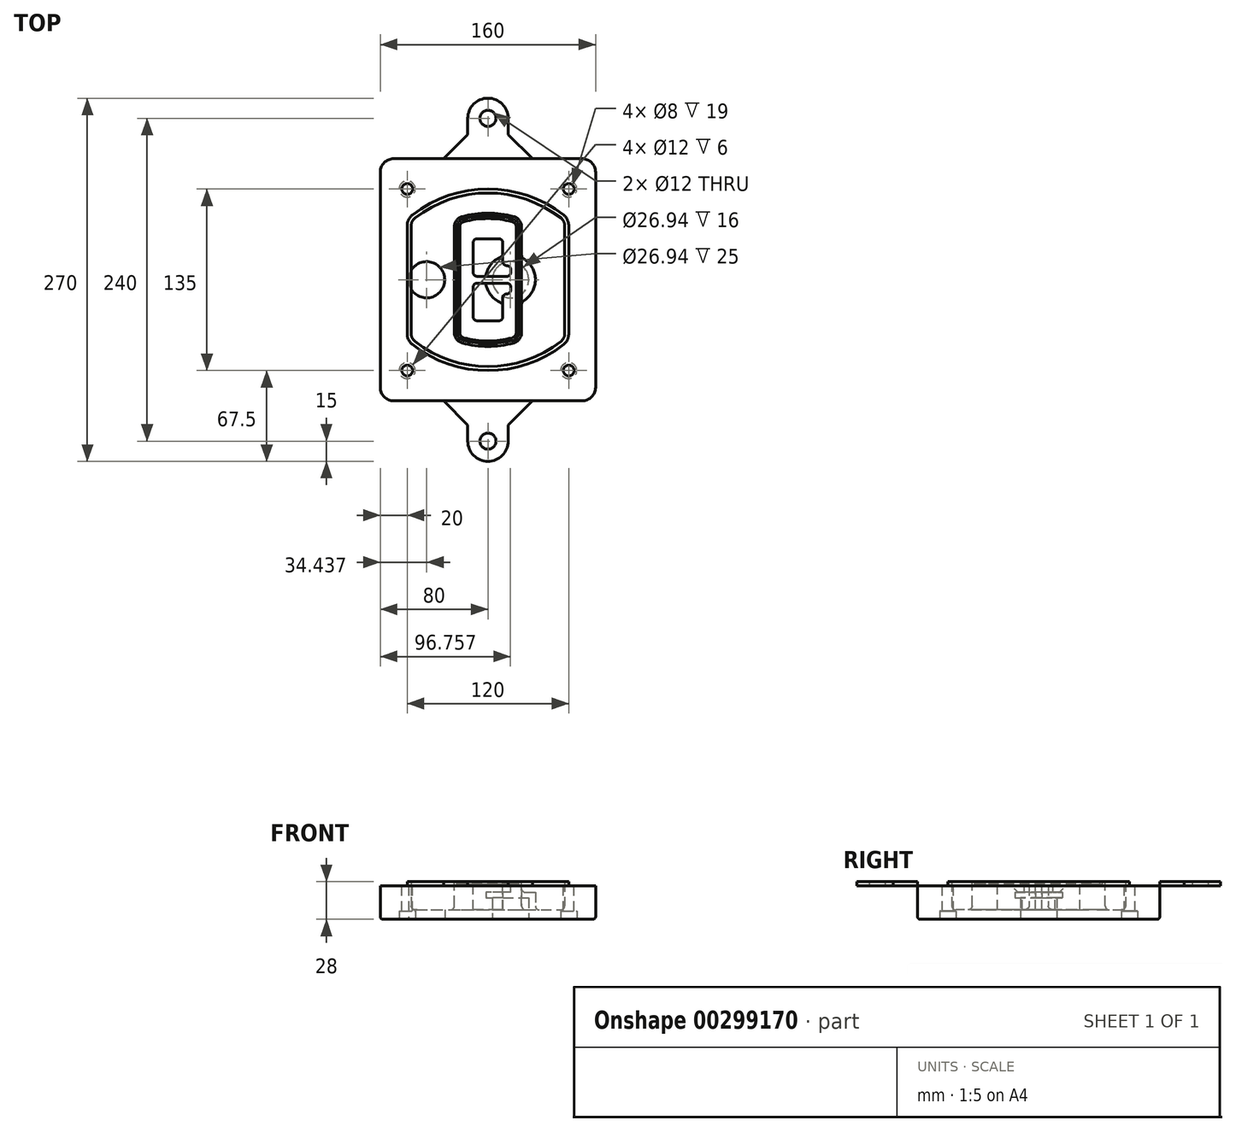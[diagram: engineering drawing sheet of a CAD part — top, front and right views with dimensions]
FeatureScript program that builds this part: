
annotation { "Feature Type Name" : "Feature", "Feature Type Description" : "" }
export const myFeature = defineFeature(function(context is Context, id is Id, definition is map)
    precondition{}
    {
        {
            var Q0;
            Q0=qCreatedBy(makeId("Top.planeOp"),FACE);
            var sketch = newSketch(context, id + "F0", { "sketchPlane" : qUnion([Q0])});
            skPoint(sketch, "E0.rect.middle", {"position": v(0, 0) * mm});
            skLineSegment(sketch, "E1.bottom", {"start": v(-70, -90) * mm, "end": v(70, -90) * mm});
            skLineSegment(sketch, "E1.top", {"start": v(-70, 90) * mm, "end": v(70, 90) * mm});
            skLineSegment(sketch, "E1.left", {"start": v(-80, -80) * mm, "end": v(-80, 80) * mm});
            skLineSegment(sketch, "E1.right", {"start": v(80, -80) * mm, "end": v(80, 80) * mm});
            skLineSegment(sketch, "E2", {"start": v(-80, 90) * mm, "end": v(80, -90) * mm, "construction": true});
            skLineSegment(sketch, "E3", {"start": v(80, 90) * mm, "end": v(-80, -90) * mm, "construction": true});
            skCircle(sketch, "E4", {"center": v(-60, 67.5) * mm, "radius": 4 * mm});
            skCircle(sketch, "E5", {"center": v(60, 67.5) * mm, "radius": 4 * mm});
            skCircle(sketch, "E6", {"center": v(60, -67.5) * mm, "radius": 4 * mm});
            skCircle(sketch, "E7", {"center": v(-60, -67.5) * mm, "radius": 4 * mm});
            skLineSegment(sketch, "E8", {"start": v(-60, 67.5) * mm, "end": v(60, 67.5) * mm, "construction": true});
            skLineSegment(sketch, "E9", {"start": v(60, 67.5) * mm, "end": v(60, -67.5) * mm, "construction": true});
            skLineSegment(sketch, "E10", {"start": v(60, -67.5) * mm, "end": v(-60, -67.5) * mm, "construction": true});
            skLineSegment(sketch, "E11", {"start": v(-60, -67.5) * mm, "end": v(-60, 67.5) * mm, "construction": true});
            skLineSegment(sketch, "E12", {"start": v(-60, 40.3) * mm, "end": v(-60, -40.3) * mm});
            skLineSegment(sketch, "E13", {"start": v(60, 40.3) * mm, "end": v(60, -40.3) * mm});
            skArc(sketch, "E14", {"start": v(56.15, 48.18) * mm, "mid": v(0, 67.5) * mm, "end": v(-56.15, 48.18) * mm});
            skArc(sketch, "E15", {"start": v(-56.15, -48.18) * mm, "mid": v(0, -67.5) * mm, "end": v(56.15, -48.18) * mm});
            skLineSegment(sketch, "E16", {"start": v(-60, 0) * mm, "end": v(60, 0) * mm, "construction": true});
            skPoint(sketch, "E17.visualSharp", {"position": v(-60, -45) * mm});
            skArc(sketch, "E17.filletArc", {"start": v(-60, -40.3) * mm, "mid": v(-58.99, -44.68) * mm, "end": v(-56.15, -48.18) * mm});
            skPoint(sketch, "E18.visualSharp", {"position": v(-60, 45) * mm});
            skArc(sketch, "E18.filletArc", {"start": v(-56.15, 48.18) * mm, "mid": v(-58.99, 44.68) * mm, "end": v(-60, 40.3) * mm});
            skPoint(sketch, "E19.visualSharp", {"position": v(60, 45) * mm});
            skArc(sketch, "E19.filletArc", {"start": v(60, 40.3) * mm, "mid": v(58.99, 44.68) * mm, "end": v(56.15, 48.18) * mm});
            skPoint(sketch, "E20.visualSharp", {"position": v(60, -45) * mm});
            skArc(sketch, "E20.filletArc", {"start": v(56.15, -48.18) * mm, "mid": v(58.99, -44.68) * mm, "end": v(60, -40.3) * mm});
            skPoint(sketch, "E21.visualSharp", {"position": v(-80, 90) * mm});
            skArc(sketch, "E21.filletArc", {"start": v(-70, 90) * mm, "mid": v(-77.07, 87.07) * mm, "end": v(-80, 80) * mm});
            skPoint(sketch, "E22.visualSharp", {"position": v(80, 90) * mm});
            skArc(sketch, "E22.filletArc", {"start": v(80, 80) * mm, "mid": v(77.07, 87.07) * mm, "end": v(70, 90) * mm});
            skPoint(sketch, "E23.visualSharp", {"position": v(80, -90) * mm});
            skArc(sketch, "E23.filletArc", {"start": v(70, -90) * mm, "mid": v(77.07, -87.07) * mm, "end": v(80, -80) * mm});
            skPoint(sketch, "E24.visualSharp", {"position": v(-80, -90) * mm});
            skArc(sketch, "E24.filletArc", {"start": v(-80, -80) * mm, "mid": v(-77.07, -87.07) * mm, "end": v(-70, -90) * mm});
            skArc(sketch, "E25.0", {"start": v(57, 40.3) * mm, "mid": v(56.3, 43.36) * mm, "end": v(54.3, 45.81) * mm});
            skLineSegment(sketch, "E25.1", {"start": v(57, 40.3) * mm, "end": v(57, -40.3) * mm});
            skArc(sketch, "E25.2", {"start": v(54.3, -45.81) * mm, "mid": v(56.3, -43.36) * mm, "end": v(57, -40.3) * mm});
            skArc(sketch, "E25.3", {"start": v(-54.3, -45.81) * mm, "mid": v(0, -64.5) * mm, "end": v(54.3, -45.81) * mm});
            skArc(sketch, "E25.4", {"start": v(-57, -40.3) * mm, "mid": v(-56.3, -43.36) * mm, "end": v(-54.3, -45.81) * mm});
            skArc(sketch, "E25.5", {"start": v(54.3, 45.81) * mm, "mid": v(0, 64.5) * mm, "end": v(-54.3, 45.81) * mm});
            skLineSegment(sketch, "E25.6", {"start": v(-57, 40.3) * mm, "end": v(-57, -40.3) * mm});
            skArc(sketch, "E25.7", {"start": v(-54.3, 45.81) * mm, "mid": v(-56.3, 43.36) * mm, "end": v(-57, 40.3) * mm});
            skArc(sketch, "E26.0", {"start": v(-58.62, 51.33) * mm, "mid": v(-62.58, 46.43) * mm, "end": v(-64, 40.3) * mm});
            skArc(sketch, "E26.1", {"start": v(58.62, 51.33) * mm, "mid": v(0, 71.5) * mm, "end": v(-58.62, 51.33) * mm});
            skArc(sketch, "E26.2", {"start": v(64, 40.3) * mm, "mid": v(62.58, 46.43) * mm, "end": v(58.62, 51.33) * mm});
            skLineSegment(sketch, "E26.3", {"start": v(64, 40.3) * mm, "end": v(64, -40.3) * mm});
            skArc(sketch, "E26.4", {"start": v(58.62, -51.33) * mm, "mid": v(62.58, -46.43) * mm, "end": v(64, -40.3) * mm});
            skLineSegment(sketch, "E26.5", {"start": v(-64, 40.3) * mm, "end": v(-64, -40.3) * mm});
            skArc(sketch, "E26.6", {"start": v(-58.62, -51.33) * mm, "mid": v(0, -71.5) * mm, "end": v(58.62, -51.33) * mm});
            skArc(sketch, "E26.7", {"start": v(-64, -40.3) * mm, "mid": v(-62.58, -46.43) * mm, "end": v(-58.62, -51.33) * mm});
            skSolve(sketch);
        }
        {
            var Q0;
            Q0=makeQuery(id+"F0.imprint","IMPRINT",FACE,{"disambiguationData":[TD([[makeQuery(id+"F0.imprint","IMPRINT",EDGE,{"derivedFrom":sQuery(id+"F0.wireOp",EDGE,"E1.bottom")}),1.0]])]});
            var Q1;
            Q1=makeQuery(id+"F0.imprint","IMPRINT",FACE,{"disambiguationData":[TD([[makeQuery(id+"F0.imprint","IMPRINT",EDGE,{"derivedFrom":sQuery(id+"F0.wireOp",EDGE,"E12")}),1.0]])]});
            var Q2;
            Q2=makeQuery(id+"F0.imprint","IMPRINT",FACE,{"disambiguationData":[TD([[makeQuery(id+"F0.imprint","IMPRINT",EDGE,{"derivedFrom":sQuery(id+"F0.wireOp",EDGE,"E25.0")}),1.0]])]});
            var Q3;
            Q3=makeQuery(id+"F0.imprint","IMPRINT",FACE,{"disambiguationData":[TD([[makeQuery(id+"F0.imprint","IMPRINT",EDGE,{"derivedFrom":sQuery(id+"F0.wireOp",EDGE,"E12")}),-1.0]])]});
            extrude(context, id + "F1", {"entities" : qUnion([Q0, Q1, Q2, Q3]), "oppositeDirection" : true, "depth" : 25 * mm});
        }
        {
            var Q0;
            Q0=makeQuery(id+"F0.imprint","IMPRINT",FACE,{"disambiguationData":[TD([[makeQuery(id+"F0.imprint","IMPRINT",EDGE,{"derivedFrom":sQuery(id+"F0.wireOp",EDGE,"E12")}),1.0]])]});
            extrude(context, id + "F2", {"entities" : qUnion([Q0]), "operationType" : NewBodyOperationType.ADD, "depth" : 3 * mm});
        }
        {
            var Q0;
            Q0=makeQuery(id+"F0.imprint","IMPRINT",FACE,{"disambiguationData":[TD([[makeQuery(id+"F0.imprint","IMPRINT",EDGE,{"derivedFrom":sQuery(id+"F0.wireOp",EDGE,"E25.0")}),1.0]])]});
            extrude(context, id + "F3", {"entities" : qUnion([Q0]), "operationType" : NewBodyOperationType.REMOVE, "oppositeDirection" : true, "depth" : 18 * mm});
        }
        {
            var Q0;
            Q0=makeQuery(id+"F2.opExtrude","CAP_FACE",FACE,{"disambiguationData":[OSD([sQuery(id+"F0.wireOp",EDGE,"E12"),sQuery(id+"F0.wireOp",EDGE,"E13"),sQuery(id+"F0.wireOp",EDGE,"E14"),sQuery(id+"F0.wireOp",EDGE,"E15"),sQuery(id+"F0.wireOp",EDGE,"E17.filletArc"),sQuery(id+"F0.wireOp",EDGE,"E18.filletArc"),sQuery(id+"F0.wireOp",EDGE,"E19.filletArc"),sQuery(id+"F0.wireOp",EDGE,"E20.filletArc"),sQuery(id+"F0.wireOp",EDGE,"E25.0"),sQuery(id+"F0.wireOp",EDGE,"E25.1"),sQuery(id+"F0.wireOp",EDGE,"E25.2"),sQuery(id+"F0.wireOp",EDGE,"E25.3"),sQuery(id+"F0.wireOp",EDGE,"E25.4"),sQuery(id+"F0.wireOp",EDGE,"E25.5"),sQuery(id+"F0.wireOp",EDGE,"E25.6"),sQuery(id+"F0.wireOp",EDGE,"E25.7")])],"isStart":false});
            var sketch = newSketch(context, id + "F4", { "sketchPlane" : qUnion([Q0])});
            skArc(sketch, "E27.0", {"start": v(-19.08, -46.97) * mm, "mid": v(0, -49.5) * mm, "end": v(19.08, -46.97) * mm});
            skArc(sketch, "E28.0", {"start": v(19.08, 46.97) * mm, "mid": v(0, 49.5) * mm, "end": v(-19.08, 46.97) * mm});
            skLineSegment(sketch, "E29", {"start": v(-25, 39.25) * mm, "end": v(-25, -39.25) * mm});
            skLineSegment(sketch, "E30", {"start": v(25, 39.25) * mm, "end": v(25, -39.25) * mm});
            skLineSegment(sketch, "E31", {"start": v(-25, 45.1) * mm, "end": v(25, 45.1) * mm, "construction": true});
            skLineSegment(sketch, "E32", {"start": v(-25, -45.1) * mm, "end": v(25, -45.1) * mm, "construction": true});
            skPoint(sketch, "E33.visualSharp", {"position": v(-25, 45.1) * mm});
            skArc(sketch, "E33.filletArc", {"start": v(-19.08, 46.97) * mm, "mid": v(-23.35, 44.11) * mm, "end": v(-25, 39.25) * mm});
            skPoint(sketch, "E34.visualSharp", {"position": v(25, 45.1) * mm});
            skArc(sketch, "E34.filletArc", {"start": v(25, 39.25) * mm, "mid": v(23.35, 44.11) * mm, "end": v(19.08, 46.97) * mm});
            skPoint(sketch, "E35.visualSharp", {"position": v(25, -45.1) * mm});
            skArc(sketch, "E35.filletArc", {"start": v(19.08, -46.97) * mm, "mid": v(23.35, -44.11) * mm, "end": v(25, -39.25) * mm});
            skPoint(sketch, "E36.visualSharp", {"position": v(-25, -45.1) * mm});
            skArc(sketch, "E36.filletArc", {"start": v(-25, -39.25) * mm, "mid": v(-23.35, -44.11) * mm, "end": v(-19.08, -46.97) * mm});
            skArc(sketch, "E37.0", {"start": v(54.3, 45.81) * mm, "mid": v(0, 64.5) * mm, "end": v(-54.3, 45.81) * mm});
            skArc(sketch, "E37.1", {"start": v(-54.3, 45.81) * mm, "mid": v(-56.3, 43.36) * mm, "end": v(-57, 40.3) * mm});
            skLineSegment(sketch, "E37.2", {"start": v(-57, 40.3) * mm, "end": v(-57, -40.3) * mm});
            skArc(sketch, "E37.3", {"start": v(-57, -40.3) * mm, "mid": v(-56.3, -43.36) * mm, "end": v(-54.3, -45.81) * mm});
            skArc(sketch, "E37.4", {"start": v(-54.3, -45.81) * mm, "mid": v(0, -64.5) * mm, "end": v(54.3, -45.81) * mm});
            skArc(sketch, "E37.5", {"start": v(54.3, -45.81) * mm, "mid": v(56.3, -43.36) * mm, "end": v(57, -40.3) * mm});
            skLineSegment(sketch, "E37.6", {"start": v(57, 40.3) * mm, "end": v(57, -40.3) * mm});
            skArc(sketch, "E37.7", {"start": v(57, 40.3) * mm, "mid": v(56.3, 43.36) * mm, "end": v(54.3, 45.81) * mm});
            skLineSegment(sketch, "E38.0", {"start": v(23, 39.25) * mm, "end": v(23, -39.25) * mm});
            skArc(sketch, "E38.1", {"start": v(18.56, -45.04) * mm, "mid": v(21.76, -42.9) * mm, "end": v(23, -39.25) * mm});
            skArc(sketch, "E38.2", {"start": v(-18.56, -45.04) * mm, "mid": v(0, -47.5) * mm, "end": v(18.56, -45.04) * mm});
            skArc(sketch, "E38.3", {"start": v(-23, -39.25) * mm, "mid": v(-21.76, -42.9) * mm, "end": v(-18.56, -45.04) * mm});
            skLineSegment(sketch, "E38.4", {"start": v(-23, 39.25) * mm, "end": v(-23, -39.25) * mm});
            skArc(sketch, "E38.5", {"start": v(23, 39.25) * mm, "mid": v(21.76, 42.9) * mm, "end": v(18.56, 45.04) * mm});
            skArc(sketch, "E38.6", {"start": v(-18.56, 45.04) * mm, "mid": v(-21.76, 42.9) * mm, "end": v(-23, 39.25) * mm});
            skArc(sketch, "E38.7", {"start": v(18.56, 45.04) * mm, "mid": v(0, 47.5) * mm, "end": v(-18.56, 45.04) * mm});
            skArc(sketch, "E39.0", {"start": v(21, 39.25) * mm, "mid": v(20.18, 41.68) * mm, "end": v(18.04, 43.1) * mm});
            skLineSegment(sketch, "E39.1", {"start": v(21, 39.25) * mm, "end": v(21, -39.25) * mm});
            skArc(sketch, "E39.2", {"start": v(18.04, -43.1) * mm, "mid": v(20.18, -41.68) * mm, "end": v(21, -39.25) * mm});
            skArc(sketch, "E39.3", {"start": v(-18.04, -43.1) * mm, "mid": v(0, -45.5) * mm, "end": v(18.04, -43.1) * mm});
            skArc(sketch, "E39.4", {"start": v(-21, -39.25) * mm, "mid": v(-20.18, -41.68) * mm, "end": v(-18.04, -43.1) * mm});
            skArc(sketch, "E39.5", {"start": v(18.04, 43.1) * mm, "mid": v(0, 45.5) * mm, "end": v(-18.04, 43.1) * mm});
            skLineSegment(sketch, "E39.6", {"start": v(-21, 39.25) * mm, "end": v(-21, -39.25) * mm});
            skArc(sketch, "E39.7", {"start": v(-18.04, 43.1) * mm, "mid": v(-20.18, 41.68) * mm, "end": v(-21, 39.25) * mm});
            skLineSegment(sketch, "E40", {"start": v(-25, 0) * mm, "end": v(25, 0) * mm, "construction": true});
            skLineSegment(sketch, "E41", {"start": v(-11, 5.5) * mm, "end": v(-11, 27.5) * mm});
            skLineSegment(sketch, "E42", {"start": v(-8, 30.5) * mm, "end": v(8, 30.5) * mm});
            skLineSegment(sketch, "E43", {"start": v(11, 27.5) * mm, "end": v(11, 13.5) * mm});
            skLineSegment(sketch, "E44", {"start": v(14, 10.5) * mm, "end": v(14, 10.5) * mm});
            skLineSegment(sketch, "E45", {"start": v(17, 7.5) * mm, "end": v(17, 5.5) * mm});
            skLineSegment(sketch, "E46", {"start": v(14, 2.5) * mm, "end": v(-8, 2.5) * mm});
            skPoint(sketch, "E47.visualSharp", {"position": v(-11, 30.5) * mm});
            skArc(sketch, "E47.filletArc", {"start": v(-8, 30.5) * mm, "mid": v(-10.12, 29.62) * mm, "end": v(-11, 27.5) * mm});
            skPoint(sketch, "E48.visualSharp", {"position": v(11, 30.5) * mm});
            skArc(sketch, "E48.filletArc", {"start": v(11, 27.5) * mm, "mid": v(10.12, 29.62) * mm, "end": v(8, 30.5) * mm});
            skPoint(sketch, "E49.visualSharp", {"position": v(11, 10.5) * mm});
            skArc(sketch, "E49.filletArc", {"start": v(11, 13.5) * mm, "mid": v(11.88, 11.38) * mm, "end": v(14, 10.5) * mm});
            skPoint(sketch, "E50.visualSharp", {"position": v(17, 10.5) * mm});
            skArc(sketch, "E50.filletArc", {"start": v(17, 7.5) * mm, "mid": v(16.12, 9.62) * mm, "end": v(14, 10.5) * mm});
            skPoint(sketch, "E51.visualSharp", {"position": v(17, 2.5) * mm});
            skArc(sketch, "E51.filletArc", {"start": v(14, 2.5) * mm, "mid": v(16.12, 3.38) * mm, "end": v(17, 5.5) * mm});
            skPoint(sketch, "E52.visualSharp", {"position": v(-11, 2.5) * mm});
            skArc(sketch, "E52.filletArc", {"start": v(-11, 5.5) * mm, "mid": v(-10.12, 3.38) * mm, "end": v(-8, 2.5) * mm});
            skLineSegment(sketch, "E53.0.MirrorCS", {"start": v(14, -2.5) * mm, "end": v(-8, -2.5) * mm});
            skArc(sketch, "E54.0.MirrorCS", {"start": v(-11, -5.5) * mm, "mid": v(-10.12, -3.38) * mm, "end": v(-8, -2.5) * mm});
            skLineSegment(sketch, "E55.0.MirrorCS", {"start": v(-11, -5.5) * mm, "end": v(-11, -27.5) * mm});
            skArc(sketch, "E56.0.MirrorCS", {"start": v(-8, -30.5) * mm, "mid": v(-10.12, -29.62) * mm, "end": v(-11, -27.5) * mm});
            skLineSegment(sketch, "E57.0.MirrorCS", {"start": v(-8, -30.5) * mm, "end": v(8, -30.5) * mm});
            skArc(sketch, "E58.0.MirrorCS", {"start": v(11, -27.5) * mm, "mid": v(10.12, -29.62) * mm, "end": v(8, -30.5) * mm});
            skLineSegment(sketch, "E59.0.MirrorCS", {"start": v(11, -27.5) * mm, "end": v(11, -13.5) * mm});
            skArc(sketch, "E60.0.MirrorCS", {"start": v(11, -13.5) * mm, "mid": v(11.88, -11.38) * mm, "end": v(14, -10.5) * mm});
            skArc(sketch, "E61.0.MirrorCS", {"start": v(17, -7.5) * mm, "mid": v(16.12, -9.62) * mm, "end": v(14, -10.5) * mm});
            skLineSegment(sketch, "E62.0.MirrorCS", {"start": v(17, -7.5) * mm, "end": v(17, -5.5) * mm});
            skArc(sketch, "E63.0.MirrorCS", {"start": v(14, -2.5) * mm, "mid": v(16.12, -3.38) * mm, "end": v(17, -5.5) * mm});
            skSolve(sketch);
        }
        {
            var Q0;
            Q0=makeQuery(id+"F4.imprint","IMPRINT",FACE,{"disambiguationData":[TD([[makeQuery(id+"F4.imprint","IMPRINT",EDGE,{"derivedFrom":sQuery(id+"F4.wireOp",EDGE,"E27.0")}),1.0]])]});
            var Q1;
            Q1=makeQuery(id+"F4.imprint","IMPRINT",FACE,{"disambiguationData":[TD([[makeQuery(id+"F4.imprint","IMPRINT",EDGE,{"derivedFrom":sQuery(id+"F4.wireOp",EDGE,"E38.0")}),-1.0]])]});
            var Q2;
            Q2=makeQuery(id+"F4.imprint","IMPRINT",FACE,{"disambiguationData":[TD([[makeQuery(id+"F4.imprint","IMPRINT",EDGE,{"derivedFrom":sQuery(id+"F4.wireOp",EDGE,"E39.0")}),1.0]])]});
            extrude(context, id + "F5", {"entities" : qUnion([Q0, Q1, Q2]), "operationType" : NewBodyOperationType.ADD, "endBound" : BoundingType.UP_TO_NEXT, "oppositeDirection" : true, "depth" : 25 * mm});
        }
        {
            var Q0;
            Q0=makeQuery(id+"F4.imprint","IMPRINT",FACE,{"disambiguationData":[TD([[makeQuery(id+"F4.imprint","IMPRINT",EDGE,{"derivedFrom":sQuery(id+"F4.wireOp",EDGE,"E38.0")}),-1.0]])]});
            extrude(context, id + "F6", {"entities" : qUnion([Q0]), "operationType" : NewBodyOperationType.REMOVE, "oppositeDirection" : true, "depth" : 2 * mm});
        }
        {
            var Q0;
            Q0=makeQuery(id+"F1.opExtrude","CAP_FACE",FACE,{"disambiguationData":[OSD([sQuery(id+"F0.wireOp",EDGE,"E1.bottom"),sQuery(id+"F0.wireOp",EDGE,"E1.top"),sQuery(id+"F0.wireOp",EDGE,"E1.left"),sQuery(id+"F0.wireOp",EDGE,"E1.right"),sQuery(id+"F0.wireOp",EDGE,"E4"),sQuery(id+"F0.wireOp",EDGE,"E5"),sQuery(id+"F0.wireOp",EDGE,"E6"),sQuery(id+"F0.wireOp",EDGE,"E7"),sQuery(id+"F0.wireOp",EDGE,"E21.filletArc"),sQuery(id+"F0.wireOp",EDGE,"E22.filletArc"),sQuery(id+"F0.wireOp",EDGE,"E23.filletArc"),sQuery(id+"F0.wireOp",EDGE,"E24.filletArc")])],"isStart":false});
            var sketch = newSketch(context, id + "F7", { "sketchPlane" : qUnion([Q0])});
            skCircle(sketch, "E64", {"center": v(16.76, 0) * mm, "radius": 13.47 * mm});
            skCircle(sketch, "E65", {"center": v(-45.56, 0) * mm, "radius": 13.47 * mm});
            skLineSegment(sketch, "E66", {"start": v(80, 0) * mm, "end": v(-80, 0) * mm});
            skCircle(sketch, "E67", {"center": v(16.76, 0) * mm, "radius": 18.47 * mm});
            skCircle(sketch, "E68", {"center": v(60, -67.5) * mm, "radius": 6 * mm});
            skCircle(sketch, "E69", {"center": v(-60, -67.5) * mm, "radius": 6 * mm});
            skCircle(sketch, "E70", {"center": v(-60, 67.5) * mm, "radius": 6 * mm});
            skCircle(sketch, "E71", {"center": v(60, 67.5) * mm, "radius": 6 * mm});
            skSolve(sketch);
        }
        {
            var Q0;
            {var subQ1=sQuery(id+"F7.wireOp",EDGE,"E66");var subQ4=sQuery(id+"F7.wireOp",EDGE,"E64");var subQ6=makeQuery(id+"F7.imprint","INTERSECT",VERTEX,{"disambiguationData":[OD(0.0)],"derivedFrom":[subQ4,subQ1]});Q0=makeQuery(id+"F7.imprint","IMPRINT",FACE,{"disambiguationData":[TD([[makeQuery(id+"F7.imprint","IMPRINT",EDGE,{"disambiguationData":[TD([[subQ6,-1.0]])],"derivedFrom":subQ4}),-1.0]])]});}
            var Q1;
            {var subQ0=sQuery(id+"F7.wireOp",EDGE,"E66");var subQ1=sQuery(id+"F7.wireOp",EDGE,"E64");var subQ3=makeQuery(id+"F7.imprint","INTERSECT",VERTEX,{"disambiguationData":[OD(0.0)],"derivedFrom":[subQ1,subQ0]});Q1=makeQuery(id+"F7.imprint","IMPRINT",FACE,{"disambiguationData":[TD([[makeQuery(id+"F7.imprint","IMPRINT",EDGE,{"disambiguationData":[TD([[subQ3,-1.0]])],"derivedFrom":subQ1}),1.0]])]});}
            var Q2;
            {var subQ0=sQuery(id+"F7.wireOp",EDGE,"E66");var subQ1=sQuery(id+"F7.wireOp",EDGE,"E64");var subQ3=makeQuery(id+"F7.imprint","INTERSECT",VERTEX,{"disambiguationData":[OD(0.0)],"derivedFrom":[subQ1,subQ0]});Q2=makeQuery(id+"F7.imprint","IMPRINT",FACE,{"disambiguationData":[TD([[makeQuery(id+"F7.imprint","IMPRINT",EDGE,{"disambiguationData":[TD([[subQ3,1.0]])],"derivedFrom":subQ1}),1.0]])]});}
            var Q3;
            {var subQ1=sQuery(id+"F7.wireOp",EDGE,"E66");var subQ4=sQuery(id+"F7.wireOp",EDGE,"E64");var subQ6=makeQuery(id+"F7.imprint","INTERSECT",VERTEX,{"disambiguationData":[OD(0.0)],"derivedFrom":[subQ4,subQ1]});Q3=makeQuery(id+"F7.imprint","IMPRINT",FACE,{"disambiguationData":[TD([[makeQuery(id+"F7.imprint","IMPRINT",EDGE,{"disambiguationData":[TD([[subQ6,1.0]])],"derivedFrom":subQ4}),-1.0]])]});}
            extrude(context, id + "F8", {"entities" : qUnion([Q0, Q1, Q2, Q3]), "operationType" : NewBodyOperationType.ADD, "oppositeDirection" : true, "depth" : 20 * mm});
        }
        {
            var Q0;
            {var subQ0=sQuery(id+"F7.wireOp",EDGE,"E66");var subQ1=sQuery(id+"F7.wireOp",EDGE,"E64");var subQ3=makeQuery(id+"F7.imprint","INTERSECT",VERTEX,{"disambiguationData":[OD(0.0)],"derivedFrom":[subQ1,subQ0]});Q0=makeQuery(id+"F7.imprint","IMPRINT",FACE,{"disambiguationData":[TD([[makeQuery(id+"F7.imprint","IMPRINT",EDGE,{"disambiguationData":[TD([[subQ3,-1.0]])],"derivedFrom":subQ1}),1.0]])]});}
            var Q1;
            {var subQ0=sQuery(id+"F7.wireOp",EDGE,"E66");var subQ1=sQuery(id+"F7.wireOp",EDGE,"E64");var subQ3=makeQuery(id+"F7.imprint","INTERSECT",VERTEX,{"disambiguationData":[OD(0.0)],"derivedFrom":[subQ1,subQ0]});Q1=makeQuery(id+"F7.imprint","IMPRINT",FACE,{"disambiguationData":[TD([[makeQuery(id+"F7.imprint","IMPRINT",EDGE,{"disambiguationData":[TD([[subQ3,1.0]])],"derivedFrom":subQ1}),1.0]])]});}
            extrude(context, id + "F9", {"entities" : qUnion([Q0, Q1]), "operationType" : NewBodyOperationType.REMOVE, "oppositeDirection" : true, "depth" : 16 * mm});
        }
        {
            var Q0;
            {var subQ0=sQuery(id+"F7.wireOp",EDGE,"E66");var subQ1=sQuery(id+"F7.wireOp",EDGE,"E65");var subQ3=makeQuery(id+"F7.imprint","INTERSECT",VERTEX,{"disambiguationData":[OD(0.0)],"derivedFrom":[subQ1,subQ0]});Q0=makeQuery(id+"F7.imprint","IMPRINT",FACE,{"disambiguationData":[TD([[makeQuery(id+"F7.imprint","IMPRINT",EDGE,{"disambiguationData":[TD([[subQ3,-1.0]])],"derivedFrom":subQ1}),1.0]])]});}
            var Q1;
            {var subQ0=sQuery(id+"F7.wireOp",EDGE,"E66");var subQ1=sQuery(id+"F7.wireOp",EDGE,"E65");var subQ3=makeQuery(id+"F7.imprint","INTERSECT",VERTEX,{"disambiguationData":[OD(0.0)],"derivedFrom":[subQ1,subQ0]});Q1=makeQuery(id+"F7.imprint","IMPRINT",FACE,{"disambiguationData":[TD([[makeQuery(id+"F7.imprint","IMPRINT",EDGE,{"disambiguationData":[TD([[subQ3,1.0]])],"derivedFrom":subQ1}),1.0]])]});}
            extrude(context, id + "F10", {"entities" : qUnion([Q0, Q1]), "operationType" : NewBodyOperationType.REMOVE, "oppositeDirection" : true, "depth" : 25 * mm});
        }
        {
            var Q0;
            Q0=makeQuery(id+"F7.imprint","IMPRINT",FACE,{"disambiguationData":[TD([[makeQuery(id+"F7.imprint","IMPRINT",EDGE,{"derivedFrom":sQuery(id+"F7.wireOp",EDGE,"E68")}),1.0]])]});
            var Q1;
            Q1=makeQuery(id+"F7.imprint","IMPRINT",FACE,{"disambiguationData":[TD([[makeQuery(id+"F7.imprint","IMPRINT",EDGE,{"derivedFrom":makeQuery(id+"F1.opExtrude","CAP_EDGE",EDGE,{"disambiguationData":[OSD([sQuery(id+"F0.wireOp",EDGE,"E5")])],"isStart":false})}),-1.0]])]});
            var Q2;
            Q2=makeQuery(id+"F7.imprint","IMPRINT",FACE,{"disambiguationData":[TD([[makeQuery(id+"F7.imprint","IMPRINT",EDGE,{"derivedFrom":sQuery(id+"F7.wireOp",EDGE,"E69")}),1.0]])]});
            var Q3;
            Q3=makeQuery(id+"F7.imprint","IMPRINT",FACE,{"disambiguationData":[TD([[makeQuery(id+"F7.imprint","IMPRINT",EDGE,{"derivedFrom":makeQuery(id+"F1.opExtrude","CAP_EDGE",EDGE,{"disambiguationData":[OSD([sQuery(id+"F0.wireOp",EDGE,"E4")])],"isStart":false})}),-1.0]])]});
            var Q4;
            Q4=makeQuery(id+"F7.imprint","IMPRINT",FACE,{"disambiguationData":[TD([[makeQuery(id+"F7.imprint","IMPRINT",EDGE,{"derivedFrom":sQuery(id+"F7.wireOp",EDGE,"E70")}),1.0]])]});
            var Q5;
            Q5=makeQuery(id+"F7.imprint","IMPRINT",FACE,{"disambiguationData":[TD([[makeQuery(id+"F7.imprint","IMPRINT",EDGE,{"derivedFrom":makeQuery(id+"F1.opExtrude","CAP_EDGE",EDGE,{"disambiguationData":[OSD([sQuery(id+"F0.wireOp",EDGE,"E7")])],"isStart":false})}),-1.0]])]});
            var Q6;
            Q6=makeQuery(id+"F7.imprint","IMPRINT",FACE,{"disambiguationData":[TD([[makeQuery(id+"F7.imprint","IMPRINT",EDGE,{"derivedFrom":sQuery(id+"F7.wireOp",EDGE,"E71")}),1.0]])]});
            var Q7;
            Q7=makeQuery(id+"F7.imprint","IMPRINT",FACE,{"disambiguationData":[TD([[makeQuery(id+"F7.imprint","IMPRINT",EDGE,{"derivedFrom":makeQuery(id+"F1.opExtrude","CAP_EDGE",EDGE,{"disambiguationData":[OSD([sQuery(id+"F0.wireOp",EDGE,"E6")])],"isStart":false})}),-1.0]])]});
            extrude(context, id + "F11", {"entities" : qUnion([Q0, Q1, Q2, Q3, Q4, Q5, Q6, Q7]), "operationType" : NewBodyOperationType.REMOVE, "oppositeDirection" : true, "depth" : 6 * mm});
        }
        {
            var Q0;
            Q0=makeQuery(id+"F9.boolean.opBoolean","COPY",FACE,{"derivedFrom":makeQuery(id+"F9.opExtrude","CAP_FACE",FACE,{"disambiguationData":[OSD([sQuery(id+"F7.wireOp",EDGE,"E64")])],"isStart":false})});
            var sketch = newSketch(context, id + "F12", { "sketchPlane" : qUnion([Q0])});
            skArc(sketch, "E72.0", {"start": v(11, 17.55) * mm, "mid": v(2.57, 11.82) * mm, "end": v(-1.54, 2.5) * mm});
            skArc(sketch, "E72.1", {"start": v(-1.54, -2.5) * mm, "mid": v(2.57, -11.82) * mm, "end": v(11, -17.55) * mm});
            skLineSegment(sketch, "E73", {"start": v(-1.54, -2.5) * mm, "end": v(14, -2.5) * mm});
            skLineSegment(sketch, "E74.0", {"start": v(14, 2.5) * mm, "end": v(-1.54, 2.5) * mm});
            skArc(sketch, "E74.1", {"start": v(14, 2.5) * mm, "mid": v(16.12, 3.38) * mm, "end": v(17, 5.5) * mm});
            skLineSegment(sketch, "E74.2", {"start": v(17, 7.5) * mm, "end": v(17, 5.5) * mm});
            skArc(sketch, "E74.3", {"start": v(17, 7.5) * mm, "mid": v(16.12, 9.62) * mm, "end": v(14, 10.5) * mm});
            skArc(sketch, "E74.4", {"start": v(11, 13.5) * mm, "mid": v(11.88, 11.38) * mm, "end": v(14, 10.5) * mm});
            skLineSegment(sketch, "E74.5", {"start": v(11, 17.55) * mm, "end": v(11, 13.5) * mm});
            skLineSegment(sketch, "E74.7", {"start": v(14, -2.5) * mm, "end": v(-1.54, -2.5) * mm});
            skArc(sketch, "E74.8", {"start": v(14, -2.5) * mm, "mid": v(16.12, -3.38) * mm, "end": v(17, -5.5) * mm});
            skLineSegment(sketch, "E74.9", {"start": v(17, -7.5) * mm, "end": v(17, -5.5) * mm});
            skArc(sketch, "E74.10", {"start": v(17, -7.5) * mm, "mid": v(16.12, -9.62) * mm, "end": v(14, -10.5) * mm});
            skArc(sketch, "E74.11", {"start": v(11, -13.5) * mm, "mid": v(11.88, -11.38) * mm, "end": v(14, -10.5) * mm});
            skLineSegment(sketch, "E74.12", {"start": v(11, -17.55) * mm, "end": v(11, -13.5) * mm});
            skPoint(sketch, "E75.orphan", {"position": v(11, -27.5) * mm});
            skPoint(sketch, "E76.orphan", {"position": v(-8, -2.5) * mm});
            skPoint(sketch, "E77.orphan", {"position": v(-8, 2.5) * mm});
            skPoint(sketch, "E78.orphan", {"position": v(11, 27.5) * mm});
            skSolve(sketch);
        }
        {
            var Q0;
            {var subQ7=sQuery(id+"F12.wireOp",EDGE,"E72.0");var subQ14=sQuery(id+"F12.wireOp",EDGE,"E72.1");var subQ16=sQuery(id+"F12.wireOp",EDGE,"E74.1");var subQ18=sQuery(id+"F12.wireOp",EDGE,"E74.8");Q0=qUnion([makeQuery(id+"F12.imprint","IMPRINT",FACE,{"disambiguationData":[TD([[makeQuery(id+"F12.imprint","IMPRINT",EDGE,{"derivedFrom":subQ7}),1.0]])]}),makeQuery(id+"F12.imprint","IMPRINT",FACE,{"disambiguationData":[TD([[makeQuery(id+"F12.imprint","IMPRINT",EDGE,{"derivedFrom":subQ14}),1.0]])]}),makeQuery(id+"F12.imprint","IMPRINT",FACE,{"disambiguationData":[TD([[makeQuery(id+"F12.imprint","IMPRINT",EDGE,{"derivedFrom":subQ16}),1.0]])]}),makeQuery(id+"F12.imprint","IMPRINT",FACE,{"disambiguationData":[TD([[makeQuery(id+"F12.imprint","IMPRINT",EDGE,{"derivedFrom":subQ18}),-1.0]])]})]);}
            var Q1;
            Q1=makeQuery(id+"F5.boolean.opBoolean","SPLIT",FACE,{"disambiguationData":[TD([makeQuery(id+"F5.opExtrude","SWEPT_FACE",FACE,{"disambiguationData":[OSD([sQuery(id+"F4.wireOp",EDGE,"E41")])]})])],"derivedFrom":makeQuery(id+"F3.boolean.opBoolean","COPY",FACE,{"derivedFrom":makeQuery(id+"F3.opExtrude","CAP_FACE",FACE,{"disambiguationData":[OSD([sQuery(id+"F0.wireOp",EDGE,"E25.0"),sQuery(id+"F0.wireOp",EDGE,"E25.1"),sQuery(id+"F0.wireOp",EDGE,"E25.2"),sQuery(id+"F0.wireOp",EDGE,"E25.3"),sQuery(id+"F0.wireOp",EDGE,"E25.4"),sQuery(id+"F0.wireOp",EDGE,"E25.5"),sQuery(id+"F0.wireOp",EDGE,"E25.6"),sQuery(id+"F0.wireOp",EDGE,"E25.7")])],"isStart":false})})});
            extrude(context, id + "F13", {"entities" : qUnion([Q0]), "operationType" : NewBodyOperationType.REMOVE, "endBound" : BoundingType.UP_TO_SURFACE, "endBoundEntityFace" : qUnion([Q1]), "depth" : 25 * mm});
        }
        {
            var Q0;
            Q0=makeQuery(id+"F3.boolean.opBoolean","COPY",EDGE,{"derivedFrom":makeQuery(id+"F3.opExtrude","CAP_EDGE",EDGE,{"disambiguationData":[OSD([sQuery(id+"F0.wireOp",EDGE,"E25.6")])],"isStart":false})});
            var Q1;
            Q1=makeQuery(id+"F8.boolean.opBoolean","INTERSECT",EDGE,{"derivedFrom":[makeQuery(id+"F5.opExtrude","SWEPT_FACE",FACE,{"disambiguationData":[OSD([sQuery(id+"F4.wireOp",EDGE,"E30")])]}),makeQuery(id+"F8.opExtrude","CAP_FACE",FACE,{"disambiguationData":[OSD([sQuery(id+"F7.wireOp",EDGE,"E67")])],"isStart":false})]});
            var Q2;
            Q2=makeQuery(id+"F8.boolean.opBoolean","INTERSECT",EDGE,{"disambiguationData":[OD(1.0)],"derivedFrom":[makeQuery(id+"F5.opExtrude","SWEPT_FACE",FACE,{"disambiguationData":[OSD([sQuery(id+"F4.wireOp",EDGE,"E30")])]}),makeQuery(id+"F8.opExtrude","SWEPT_FACE",FACE,{"disambiguationData":[OSD([sQuery(id+"F7.wireOp",EDGE,"E67")])]})]});
            var Q3;
            {var subQ0=sQuery(id+"F4.wireOp",EDGE,"E30");Q3=makeQuery(id+"F8.boolean.opBoolean","SPLIT",EDGE,{"disambiguationData":[TD([makeQuery(id+"F5.opExtrude","SWEPT_FACE",FACE,{"disambiguationData":[OSD([sQuery(id+"F4.wireOp",EDGE,"E35.filletArc")])]})])],"derivedFrom":makeQuery(id+"F5.opExtrude","CAP_EDGE",EDGE,{"disambiguationData":[OSD([subQ0])],"isStart":false})});}
            var Q4;
            {var subQ0=sQuery(id+"F0.wireOp",EDGE,"E25.7");var subQ1=sQuery(id+"F0.wireOp",EDGE,"E25.1");var subQ2=sQuery(id+"F0.wireOp",EDGE,"E25.6");var subQ3=sQuery(id+"F0.wireOp",EDGE,"E25.5");var subQ4=sQuery(id+"F0.wireOp",EDGE,"E25.4");var subQ5=sQuery(id+"F0.wireOp",EDGE,"E25.0");var subQ6=sQuery(id+"F0.wireOp",EDGE,"E25.2");var subQ7=sQuery(id+"F0.wireOp",EDGE,"E25.3");Q4=makeQuery(id+"F8.boolean.opBoolean","INTERSECT",EDGE,{"derivedFrom":[makeQuery(id+"F5.boolean.opBoolean","SPLIT",FACE,{"disambiguationData":[TD([makeQuery(id+"F2.opExtrude","SWEPT_FACE",FACE,{"disambiguationData":[OSD([subQ5])]})])],"derivedFrom":makeQuery(id+"F3.boolean.opBoolean","COPY",FACE,{"derivedFrom":makeQuery(id+"F3.opExtrude","CAP_FACE",FACE,{"disambiguationData":[OSD([subQ5,subQ1,subQ6,subQ7,subQ4,subQ3,subQ2,subQ0])],"isStart":false})})}),makeQuery(id+"F8.opExtrude","SWEPT_FACE",FACE,{"disambiguationData":[OSD([sQuery(id+"F7.wireOp",EDGE,"E67")])]})]});}
            var Q5;
            Q5=makeQuery(id+"F8.boolean.opBoolean","INTERSECT",EDGE,{"disambiguationData":[OD(0.0)],"derivedFrom":[makeQuery(id+"F5.opExtrude","SWEPT_FACE",FACE,{"disambiguationData":[OSD([sQuery(id+"F4.wireOp",EDGE,"E30")])]}),makeQuery(id+"F8.opExtrude","SWEPT_FACE",FACE,{"disambiguationData":[OSD([sQuery(id+"F7.wireOp",EDGE,"E67")])]})]});
            fillet(context, id + "F14", {"entities" : qUnion([Q0, Q1, Q2, Q3, Q4, Q5]), "radius" : 3 * mm, "tangentPropagation" : true, "allowEdgeOverflow" : false});
        }
        {
            var Q0;
            Q0=makeQuery(id+"F1.opExtrude","CAP_EDGE",EDGE,{"disambiguationData":[OSD([sQuery(id+"F0.wireOp",EDGE,"E1.bottom")])],"isStart":false});
            fillet(context, id + "F15", {"entities" : qUnion([Q0]), "radius" : 2 * mm, "tangentPropagation" : true, "allowEdgeOverflow" : false});
        }
        {
            var Q0;
            {var subQ0=sQuery(id+"F0.wireOp",EDGE,"E21.filletArc");var subQ1=sQuery(id+"F0.wireOp",EDGE,"E7");var subQ2=sQuery(id+"F0.wireOp",EDGE,"E6");var subQ3=sQuery(id+"F0.wireOp",EDGE,"E5");var subQ4=sQuery(id+"F0.wireOp",EDGE,"E4");var subQ5=sQuery(id+"F0.wireOp",EDGE,"E22.filletArc");var subQ6=sQuery(id+"F0.wireOp",EDGE,"E1.bottom");var subQ7=sQuery(id+"F0.wireOp",EDGE,"E1.right");var subQ8=sQuery(id+"F0.wireOp",EDGE,"E1.top");var subQ9=sQuery(id+"F0.wireOp",EDGE,"E1.left");var subQ10=sQuery(id+"F0.wireOp",EDGE,"E23.filletArc");var subQ11=sQuery(id+"F0.wireOp",EDGE,"E24.filletArc");Q0=makeQuery(id+"F2.boolean.opBoolean","SPLIT",FACE,{"disambiguationData":[TD([makeQuery(id+"F1.opExtrude","SWEPT_FACE",FACE,{"disambiguationData":[OSD([subQ6])]})])],"derivedFrom":makeQuery(id+"F1.opExtrude","CAP_FACE",FACE,{"disambiguationData":[OSD([subQ6,subQ8,subQ9,subQ7,subQ4,subQ3,subQ2,subQ1,subQ0,subQ5,subQ10,subQ11])],"isStart":true})});}
            var sketch = newSketch(context, id + "F16", { "sketchPlane" : qUnion([Q0])});
            skLineSegment(sketch, "E79", {"start": v(0, 90) * mm, "end": v(0, 120) * mm, "construction": true});
            skCircle(sketch, "E80", {"center": v(0, 120) * mm, "radius": 6 * mm});
            skArc(sketch, "E81", {"start": v(15, 120) * mm, "mid": v(0, 135) * mm, "end": v(-15, 120) * mm});
            skLineSegment(sketch, "E82", {"start": v(-15, 120) * mm, "end": v(-15, 108) * mm});
            skLineSegment(sketch, "E83", {"start": v(-15, 108) * mm, "end": v(-33, 90) * mm});
            skLineSegment(sketch, "E84", {"start": v(15, 120) * mm, "end": v(15, 108) * mm});
            skLineSegment(sketch, "E85", {"start": v(15, 108) * mm, "end": v(33, 90) * mm});
            skLineSegment(sketch, "E86", {"start": v(-140.07, 0) * mm, "end": v(141.47, 0) * mm, "construction": true});
            skPoint(sketch, "E86.endSnap0", {"position": v(80, 0) * mm});
            skLineSegment(sketch, "E87.MirrorCS", {"start": v(15, -120) * mm, "end": v(15, -108) * mm});
            skLineSegment(sketch, "E88.MirrorCS", {"start": v(-15, -120) * mm, "end": v(-15, -108) * mm});
            skArc(sketch, "E89.MirrorCS", {"start": v(15, -120) * mm, "mid": v(0, -135) * mm, "end": v(-15, -120) * mm});
            skCircle(sketch, "E90.MirrorC", {"center": v(0, -120) * mm, "radius": 6 * mm});
            skLineSegment(sketch, "E91.MirrorCS", {"start": v(-15, -108) * mm, "end": v(-33, -90) * mm});
            skLineSegment(sketch, "E92.MirrorCS", {"start": v(15, -108) * mm, "end": v(33, -90) * mm});
            skSolve(sketch);
        }
        {
            var Q0;
            Q0=makeQuery(id+"F16.imprint","IMPRINT",FACE,{"disambiguationData":[TD([[makeQuery(id+"F16.imprint","IMPRINT",EDGE,{"derivedFrom":sQuery(id+"F16.wireOp",EDGE,"E80")}),-1.0]])]});
            var Q1;
            Q1=makeQuery(id+"F16.imprint","IMPRINT",FACE,{"disambiguationData":[TD([[makeQuery(id+"F16.imprint","IMPRINT",EDGE,{"derivedFrom":sQuery(id+"F16.wireOp",EDGE,"3e1da879-6425-481b-9631-7aad7a5b017c0.MirrorC")}),1.0]])]});
            var Q2;
            Q2=makeQuery(id+"F2.opExtrude","CAP_FACE",FACE,{"disambiguationData":[OSD([sQuery(id+"F0.wireOp",EDGE,"E12"),sQuery(id+"F0.wireOp",EDGE,"E13"),sQuery(id+"F0.wireOp",EDGE,"E14"),sQuery(id+"F0.wireOp",EDGE,"E15"),sQuery(id+"F0.wireOp",EDGE,"E17.filletArc"),sQuery(id+"F0.wireOp",EDGE,"E18.filletArc"),sQuery(id+"F0.wireOp",EDGE,"E19.filletArc"),sQuery(id+"F0.wireOp",EDGE,"E20.filletArc"),sQuery(id+"F0.wireOp",EDGE,"E25.0"),sQuery(id+"F0.wireOp",EDGE,"E25.1"),sQuery(id+"F0.wireOp",EDGE,"E25.2"),sQuery(id+"F0.wireOp",EDGE,"E25.3"),sQuery(id+"F0.wireOp",EDGE,"E25.4"),sQuery(id+"F0.wireOp",EDGE,"E25.5"),sQuery(id+"F0.wireOp",EDGE,"E25.6"),sQuery(id+"F0.wireOp",EDGE,"E25.7")])],"isStart":false});
            extrude(context, id + "F17", {"entities" : qUnion([Q0, Q1]), "endBound" : BoundingType.UP_TO_SURFACE, "endBoundEntityFace" : qUnion([Q2]), "depth" : 25 * mm});
        }
        {
            var Q0;
            Q0=makeQuery(id+"F16.imprint","IMPRINT",FACE,{"disambiguationData":[TD([[makeQuery(id+"F16.imprint","IMPRINT",EDGE,{"derivedFrom":sQuery(id+"F16.wireOp",EDGE,"E87.MirrorCS")}),1.0]])]});
            var Q1;
            Q1=makeQuery(id+"F2.opExtrude","CAP_FACE",FACE,{"disambiguationData":[OSD([sQuery(id+"F0.wireOp",EDGE,"E12"),sQuery(id+"F0.wireOp",EDGE,"E13"),sQuery(id+"F0.wireOp",EDGE,"E14"),sQuery(id+"F0.wireOp",EDGE,"E15"),sQuery(id+"F0.wireOp",EDGE,"E17.filletArc"),sQuery(id+"F0.wireOp",EDGE,"E18.filletArc"),sQuery(id+"F0.wireOp",EDGE,"E19.filletArc"),sQuery(id+"F0.wireOp",EDGE,"E20.filletArc"),sQuery(id+"F0.wireOp",EDGE,"E25.0"),sQuery(id+"F0.wireOp",EDGE,"E25.1"),sQuery(id+"F0.wireOp",EDGE,"E25.2"),sQuery(id+"F0.wireOp",EDGE,"E25.3"),sQuery(id+"F0.wireOp",EDGE,"E25.4"),sQuery(id+"F0.wireOp",EDGE,"E25.5"),sQuery(id+"F0.wireOp",EDGE,"E25.6"),sQuery(id+"F0.wireOp",EDGE,"E25.7")])],"isStart":false});
            extrude(context, id + "F18", {"entities" : qUnion([Q0]), "endBound" : BoundingType.UP_TO_SURFACE, "endBoundEntityFace" : qUnion([Q1]), "depth" : 25 * mm});
        }
    });
